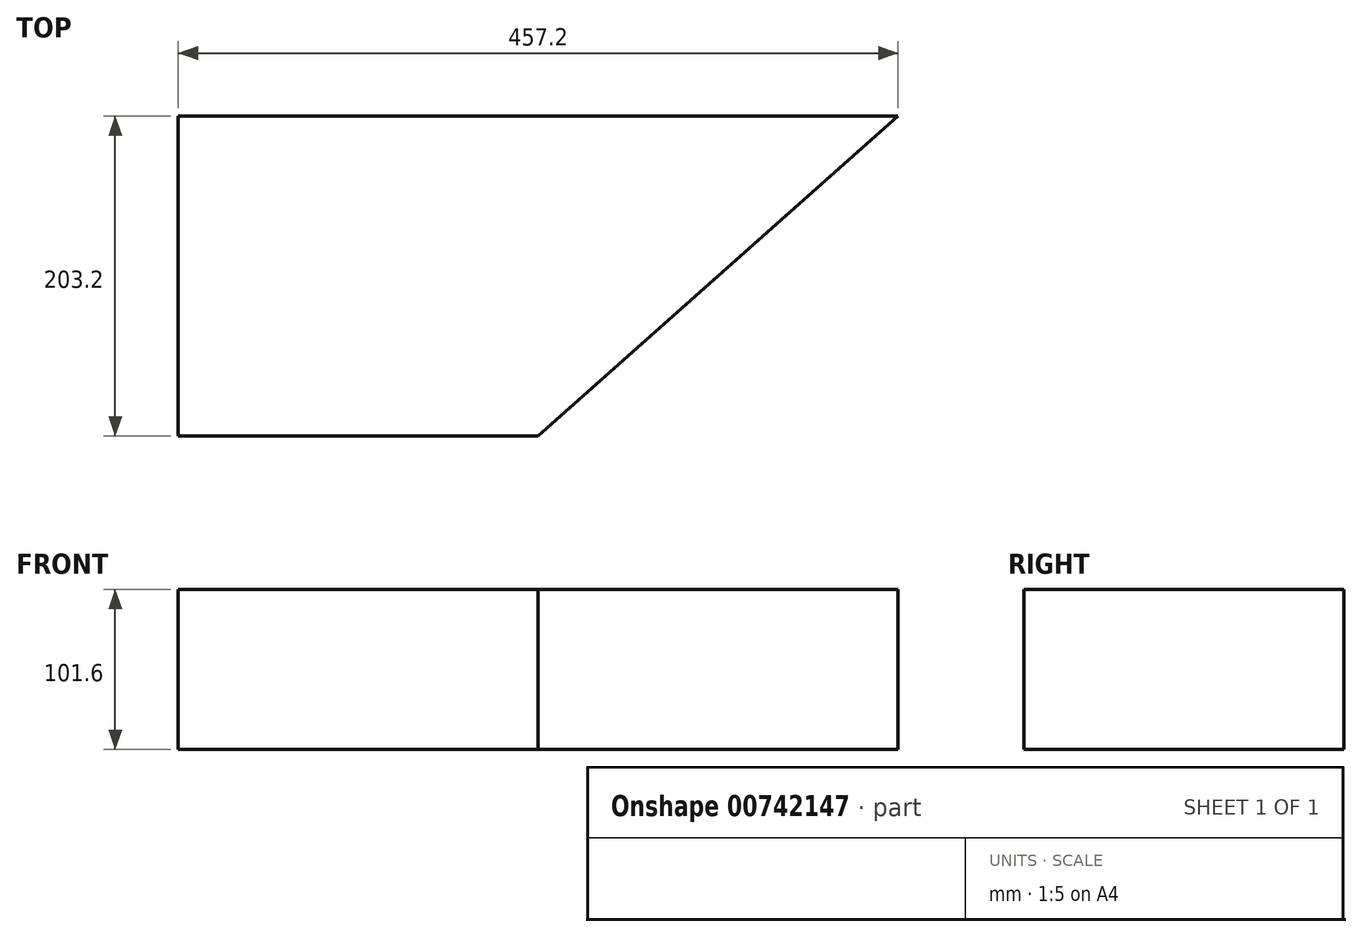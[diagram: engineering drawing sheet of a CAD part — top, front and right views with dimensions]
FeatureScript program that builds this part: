
annotation { "Feature Type Name" : "Feature", "Feature Type Description" : "" }
export const myFeature = defineFeature(function(context is Context, id is Id, definition is map)
    precondition{}
    {
        {
            var Q0;
            Q0=qCreatedBy(makeId("Top.planeOp"),FACE);
            var sketch = newSketch(context, id + "F0", { "sketchPlane" : qUnion([Q0])});
            skLineSegment(sketch, "E0", {"start": v(0, 0) * mm, "end": v(0, -203.2) * mm});
            skLineSegment(sketch, "E1", {"start": v(0, -203.2) * mm, "end": v(228.6, -203.2) * mm});
            skLineSegment(sketch, "E2", {"start": v(228.6, -203.2) * mm, "end": v(457.2, 0) * mm});
            skLineSegment(sketch, "E3", {"start": v(457.2, 0) * mm, "end": v(0, 0) * mm});
            skSolve(sketch);
        }
        {
            var Q0;
            Q0=makeQuery(id+"F0.imprint","IMPRINT",FACE,{"disambiguationData":[TD([[makeQuery(id+"F0.imprint","IMPRINT",EDGE,{"derivedFrom":sQuery(id+"F0.wireOp",EDGE,"E0")}),1.0]])]});
            extrude(context, id + "F1", {"entities" : qUnion([Q0]), "depth" : 101.6 * mm, "offsetDistance" : 25.4 * mm});
        }
    });
